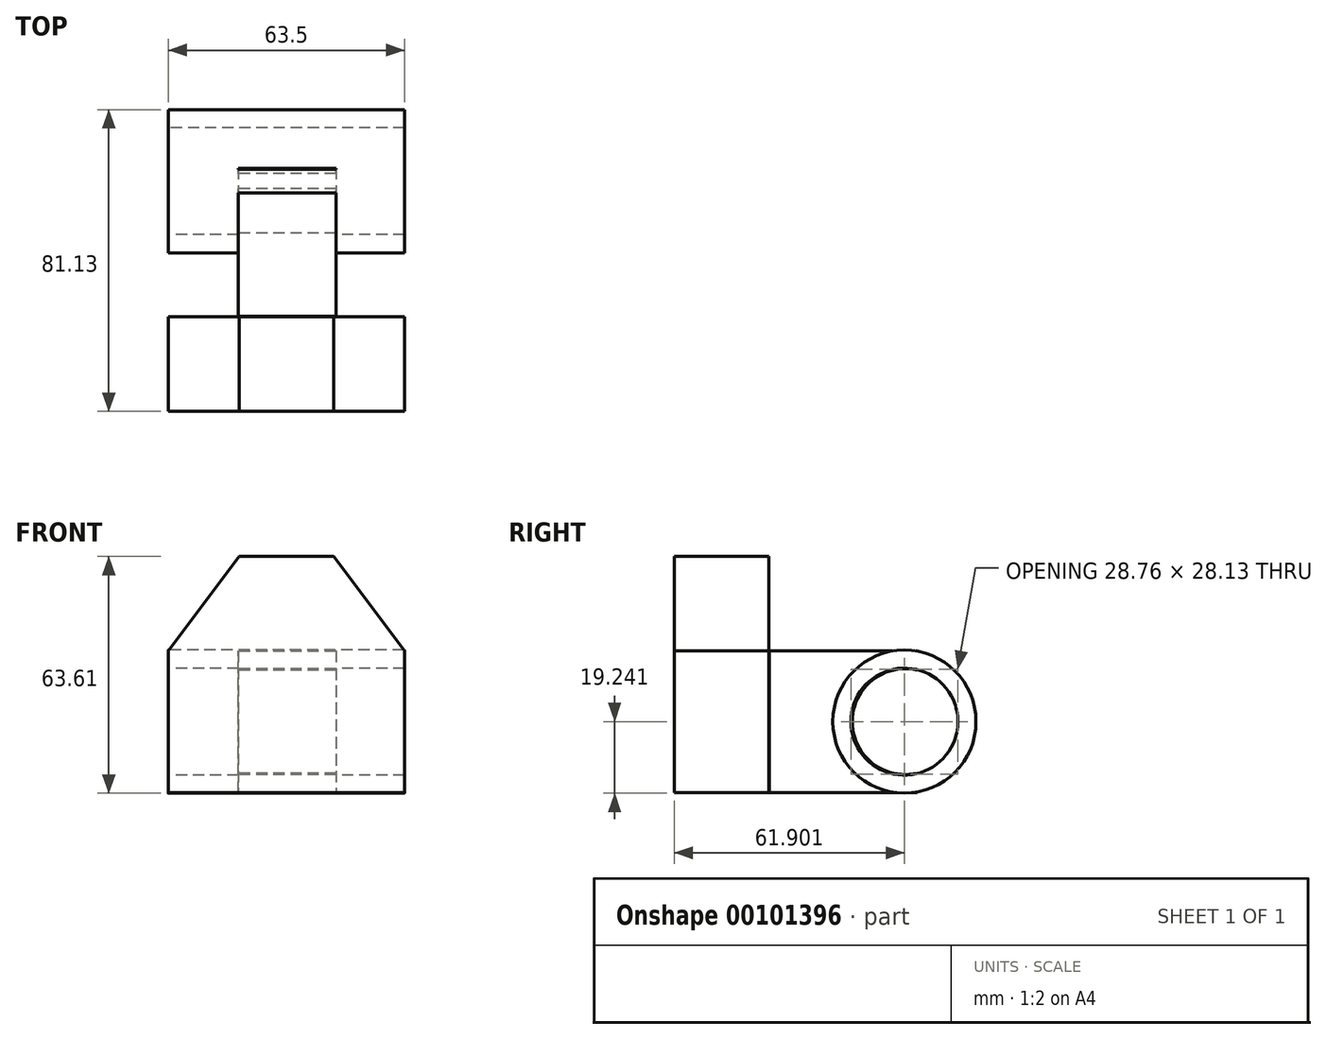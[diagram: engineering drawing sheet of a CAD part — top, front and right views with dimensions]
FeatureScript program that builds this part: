
annotation { "Feature Type Name" : "Feature", "Feature Type Description" : "" }
export const myFeature = defineFeature(function(context is Context, id is Id, definition is map)
    precondition{}
    {
        {
            var Q0;
            Q0=qCreatedBy(makeId("Front.planeOp"),FACE);
            var sketch = newSketch(context, id + "F0", { "sketchPlane" : qUnion([Q0])});
            skLineSegment(sketch, "E0", {"start": v(0, 0) * mm, "end": v(0, 38.1) * mm});
            skLineSegment(sketch, "E1", {"start": v(63.5, 38.1) * mm, "end": v(63.5, 0) * mm});
            skLineSegment(sketch, "E2", {"start": v(63.5, 0) * mm, "end": v(0, 0) * mm});
            skLineSegment(sketch, "E3", {"start": v(0, 38.1) * mm, "end": v(19.05, 63.5) * mm});
            skLineSegment(sketch, "E4", {"start": v(19.05, 63.5) * mm, "end": v(44.45, 63.5) * mm});
            skLineSegment(sketch, "E5", {"start": v(44.45, 63.5) * mm, "end": v(63.5, 38.1) * mm});
            skSolve(sketch);
        }
        {
            var Q0;
            Q0=qCreatedBy(makeId("Right.planeOp"),FACE);
            var sketch = newSketch(context, id + "F1", { "sketchPlane" : qUnion([Q0])});
            skCircle(sketch, "E6", {"center": v(49.2, 19.13) * mm, "radius": 19.24 * mm});
            skCircle(sketch, "E7", {"center": v(49.2, 19.13) * mm, "radius": 14.37 * mm});
            skSolve(sketch);
        }
        {
            var Q0;
            Q0 = qSketchRegion(id + "F0", true);
            extrude(context, id + "F2", {"entities" : qUnion([Q0]), "endBound" : BoundingType.SYMMETRIC, "depth" : 25.4 * mm});
        }
        {
            var Q0;
            Q0=makeQuery(id+"F1.imprint","IMPRINT",FACE,{"disambiguationData":[TD([[makeQuery(id+"F1.imprint","IMPRINT",EDGE,{"derivedFrom":sQuery(id+"F1.wireOp",EDGE,"E6")}),1.0]])]});
            extrude(context, id + "F3", {"entities" : qUnion([Q0]), "depth" : 63.5 * mm});
        }
        {
            var Q0;
            Q0=qCreatedBy(makeId("Top.planeOp"),FACE);
            var sketch = newSketch(context, id + "F4", { "sketchPlane" : qUnion([Q0])});
            skLineSegment(sketch, "E8", {"start": v(18.85, 12.91) * mm, "end": v(18.85, 52.68) * mm});
            skLineSegment(sketch, "E9", {"start": v(18.85, 52.68) * mm, "end": v(45.05, 52.68) * mm});
            skLineSegment(sketch, "E10", {"start": v(45.05, 52.68) * mm, "end": v(45.05, 12.91) * mm});
            skLineSegment(sketch, "E11", {"start": v(45.05, 12.91) * mm, "end": v(18.85, 12.91) * mm});
            skSolve(sketch);
        }
        {
            var Q0;
            Q0 = qSketchRegion(id + "F4", true);
            extrude(context, id + "F5", {"entities" : qUnion([Q0]), "operationType" : NewBodyOperationType.ADD, "depth" : 38.1 * mm});
        }
        {
            var Q0;
            Q0=qCreatedBy(makeId("Right.planeOp"),FACE);
            var sketch = newSketch(context, id + "F6", { "sketchPlane" : qUnion([Q0])});
            skCircle(sketch, "E12", {"center": v(49.38, 19.13) * mm, "radius": 14.2 * mm});
            skSolve(sketch);
        }
        {
            var Q0;
            Q0 = qSketchRegion(id + "F6", true);
            extrude(context, id + "F7", {"entities" : qUnion([Q0]), "operationType" : NewBodyOperationType.REMOVE, "endBound" : BoundingType.THROUGH_ALL, "depth" : 25.4 * mm});
        }
    });
